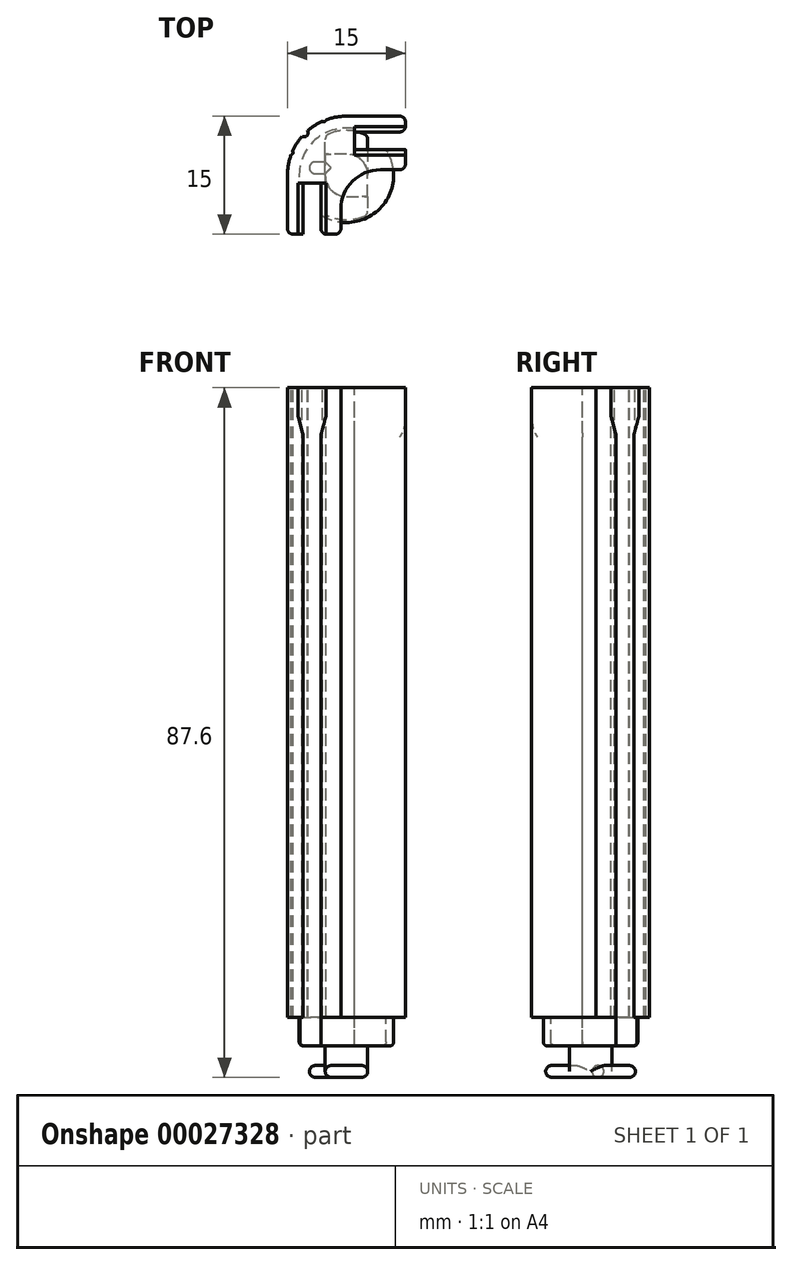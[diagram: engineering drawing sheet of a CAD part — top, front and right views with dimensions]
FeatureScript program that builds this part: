
annotation { "Feature Type Name" : "Feature", "Feature Type Description" : "" }
export const myFeature = defineFeature(function(context is Context, id is Id, definition is map)
    precondition{}
    {
        {
            var Q0;
            Q0=qCreatedBy(makeId("Top.planeOp"),FACE);
            var sketch = newSketch(context, id + "F0", { "sketchPlane" : qUnion([Q0])});
            skLineSegment(sketch, "E0", {"start": v(-7.5, -7.5) * mm, "end": v(-0.7, -7.5) * mm});
            skLineSegment(sketch, "E1", {"start": v(7.5, 0.7) * mm, "end": v(7.5, 7.5) * mm});
            skLineSegment(sketch, "E2", {"start": v(-0.7, -7.5) * mm, "end": v(-0.7, -4.3) * mm});
            skLineSegment(sketch, "E3", {"start": v(4.3, 0.7) * mm, "end": v(7.5, 0.7) * mm});
            skArc(sketch, "E4.filletArc", {"start": v(4.3, 0.7) * mm, "mid": v(0.76, -0.76) * mm, "end": v(-0.7, -4.3) * mm});
            skLineSegment(sketch, "E5", {"start": v(-7.5, -7.5) * mm, "end": v(-7.5, 0) * mm});
            skLineSegment(sketch, "E6", {"start": v(0, 7.5) * mm, "end": v(7.5, 7.5) * mm});
            skArc(sketch, "E7.filletArc", {"start": v(0, 7.5) * mm, "mid": v(-5.3, 5.3) * mm, "end": v(-7.5, 0) * mm});
            skSolve(sketch);
        }
        {
            var Q0;
            Q0 = qSketchRegion(id + "F0", true);
            extrude(context, id + "F1", {"entities" : qUnion([Q0]), "depth" : 80 * mm});
        }
        {
            var Q0;
            Q0=makeQuery(id+"F1.opExtrude","SWEPT_FACE",FACE,{"disambiguationData":[OSD([sQuery(id+"F0.wireOp",EDGE,"E0")])]});
            var sketch = newSketch(context, id + "F2", { "sketchPlane" : qUnion([Q0])});
            skLineSegment(sketch, "E8", {"start": v(-3.25, 0) * mm, "end": v(-3.25, 73.73) * mm});
            skLineSegment(sketch, "E9", {"start": v(-3.18, 74.26) * mm, "end": v(-2.64, 76.24) * mm});
            skLineSegment(sketch, "E10", {"start": v(-2.57, 76.77) * mm, "end": v(-2.57, 80) * mm});
            skPoint(sketch, "E11.visualSharp", {"position": v(-3.25, 74) * mm});
            skArc(sketch, "E11.filletArc", {"start": v(-3.18, 74.26) * mm, "mid": v(-3.23, 74) * mm, "end": v(-3.25, 73.73) * mm});
            skPoint(sketch, "E12.visualSharp", {"position": v(-2.57, 76.5) * mm});
            skArc(sketch, "E12.filletArc", {"start": v(-2.64, 76.24) * mm, "mid": v(-2.6, 76.5) * mm, "end": v(-2.57, 76.77) * mm});
            skLineSegment(sketch, "E13", {"start": v(-5.5, 0) * mm, "end": v(-3.25, 0) * mm});
            skLineSegment(sketch, "E14", {"start": v(-3.25, 0) * mm, "end": v(-5.5, 0) * mm});
            skLineSegment(sketch, "E15", {"start": v(-4.37, 0) * mm, "end": v(-4.37, 80) * mm, "construction": true});
            skLineSegment(sketch, "E16.MirrorCS", {"start": v(-5.5, 0) * mm, "end": v(-5.5, 73.73) * mm});
            skArc(sketch, "E17.MirrorCS", {"start": v(-5.57, 74.26) * mm, "mid": v(-5.52, 74) * mm, "end": v(-5.5, 73.73) * mm});
            skArc(sketch, "E18.MirrorCS", {"start": v(-6.1, 76.24) * mm, "mid": v(-6.16, 76.5) * mm, "end": v(-6.17, 76.77) * mm});
            skPoint(sketch, "E19.MirrorP", {"position": v(-5.5, 74) * mm});
            skPoint(sketch, "E20.MirrorP", {"position": v(-6.17, 76.5) * mm});
            skLineSegment(sketch, "E21.MirrorCS", {"start": v(-6.17, 76.77) * mm, "end": v(-6.17, 80) * mm});
            skLineSegment(sketch, "E22.MirrorCS", {"start": v(-5.57, 74.26) * mm, "end": v(-6.1, 76.24) * mm});
            skSolve(sketch);
        }
        {
            var Q0;
            Q0=makeQuery(id+"F2.imprint","IMPRINT",FACE,{"disambiguationData":[TD([[makeQuery(id+"F2.imprint","IMPRINT",EDGE,{"derivedFrom":sQuery(id+"F2.wireOp",EDGE,"E8")}),1.0]])]});
            extrude(context, id + "F3", {"entities" : qUnion([Q0]), "operationType" : NewBodyOperationType.REMOVE, "oppositeDirection" : true, "depth" : 6.5 * mm});
        }
        {
            var Q0;
            Q0=makeQuery(id+"F1.opExtrude","SWEPT_EDGE",EDGE,{"disambiguationData":[OSD([sQuery(id+"F0.wireOp",EDGE,"E0"),sQuery(id+"F0.wireOp",EDGE,"E2")])]});
            var Q1;
            Q1=makeQuery(id+"F3.boolean.opBoolean","COPY",EDGE,{"derivedFrom":makeQuery(id+"F3.opExtrude","CAP_EDGE",EDGE,{"disambiguationData":[OSD([sQuery(id+"F2.wireOp",EDGE,"E8")])],"isStart":true})});
            var Q2;
            Q2=makeQuery(id+"F3.boolean.opBoolean","COPY",EDGE,{"derivedFrom":makeQuery(id+"F3.opExtrude","CAP_EDGE",EDGE,{"disambiguationData":[OSD([sQuery(id+"F2.wireOp",EDGE,"60f27833-4f76-45b9-a807-f1616053afc30.MirrorCS")])],"isStart":true})});
            var Q3;
            Q3=makeQuery(id+"F1.opExtrude","SWEPT_EDGE",EDGE,{"disambiguationData":[OSD([sQuery(id+"F0.wireOp",EDGE,"E0"),sQuery(id+"F0.wireOp",EDGE,"E5")])]});
            var Q4;
            Q4=makeQuery(id+"F3.boolean.opBoolean","COPY",EDGE,{"derivedFrom":makeQuery(id+"F3.opExtrude","CAP_EDGE",EDGE,{"disambiguationData":[OSD([sQuery(id+"F2.wireOp",EDGE,"E16.MirrorCS")])],"isStart":true})});
            fillet(context, id + "F4", {"entities" : qUnion([Q0, Q1, Q2, Q3, Q4]), "radius" : 0.75 * mm, "allowEdgeOverflow" : false});
        }
        {
            var Q0;
            Q0=makeQuery(id+"F1.opExtrude","SWEPT_FACE",FACE,{"disambiguationData":[OSD([sQuery(id+"F0.wireOp",EDGE,"E1")])]});
            var sketch = newSketch(context, id + "F5", { "sketchPlane" : qUnion([Q0])});
            skLineSegment(sketch, "E23.MirrorCS", {"start": v(3.18, 74.26) * mm, "end": v(2.64, 76.24) * mm});
            skPoint(sketch, "E24.MirrorP", {"position": v(3.25, 74) * mm});
            skPoint(sketch, "E25.MirrorP", {"position": v(2.57, 76.5) * mm});
            skLineSegment(sketch, "E26.MirrorCS", {"start": v(2.57, 76.77) * mm, "end": v(2.57, 80) * mm});
            skLineSegment(sketch, "E27", {"start": v(5.57, 74.26) * mm, "end": v(6.1, 76.24) * mm});
            skLineSegment(sketch, "E28", {"start": v(6.18, 76.77) * mm, "end": v(6.18, 80) * mm});
            skPoint(sketch, "E29.visualSharp", {"position": v(5.5, 74) * mm});
            skPoint(sketch, "E30.visualSharp", {"position": v(6.18, 76.5) * mm});
            skArc(sketch, "E31.MirrorCS", {"start": v(3.18, 74.26) * mm, "mid": v(3.23, 74) * mm, "end": v(3.25, 73.73) * mm});
            skArc(sketch, "E32.MirrorCS", {"start": v(2.64, 76.24) * mm, "mid": v(2.6, 76.5) * mm, "end": v(2.57, 76.77) * mm});
            skArc(sketch, "E30.filletArc", {"start": v(6.1, 76.24) * mm, "mid": v(6.16, 76.5) * mm, "end": v(6.18, 76.77) * mm});
            skArc(sketch, "E29.filletArc", {"start": v(5.57, 74.26) * mm, "mid": v(5.52, 74) * mm, "end": v(5.5, 73.73) * mm});
            skLineSegment(sketch, "E33", {"start": v(5.5, 0) * mm, "end": v(5.5, 73.73) * mm});
            skLineSegment(sketch, "E34", {"start": v(4.38, 0) * mm, "end": v(4.38, 24.5) * mm, "construction": true});
            skLineSegment(sketch, "E35.MirrorCS", {"start": v(3.25, 0) * mm, "end": v(3.25, 73.73) * mm});
            skLineSegment(sketch, "E36", {"start": v(5.5, 0) * mm, "end": v(3.25, 0) * mm});
            skLineSegment(sketch, "E37", {"start": v(3.25, 0) * mm, "end": v(5.5, 0) * mm});
            skSolve(sketch);
        }
        {
            var Q0;
            Q0=makeQuery(id+"F5.imprint","IMPRINT",FACE,{"disambiguationData":[TD([[makeQuery(id+"F5.imprint","IMPRINT",EDGE,{"derivedFrom":sQuery(id+"F5.wireOp",EDGE,"E23.MirrorCS")}),-1.0]])]});
            extrude(context, id + "F6", {"entities" : qUnion([Q0]), "operationType" : NewBodyOperationType.REMOVE, "oppositeDirection" : true, "depth" : 6.5 * mm});
        }
        {
            var Q0;
            Q0=makeQuery(id+"F1.opExtrude","SWEPT_EDGE",EDGE,{"disambiguationData":[OSD([sQuery(id+"F0.wireOp",EDGE,"E1"),sQuery(id+"F0.wireOp",EDGE,"E3")])]});
            var Q1;
            Q1=makeQuery(id+"F6.boolean.opBoolean","COPY",EDGE,{"derivedFrom":makeQuery(id+"F6.opExtrude","CAP_EDGE",EDGE,{"disambiguationData":[OSD([sQuery(id+"F5.wireOp",EDGE,"fac70760-1ccf-4664-8ab7-3cb3c320e3f2.MirrorCS")])],"isStart":true})});
            var Q2;
            Q2=makeQuery(id+"F6.boolean.opBoolean","COPY",EDGE,{"derivedFrom":makeQuery(id+"F6.opExtrude","CAP_EDGE",EDGE,{"disambiguationData":[OSD([sQuery(id+"F5.wireOp",EDGE,"9f08e8bf-f9da-4fc2-9655-82f690379f85")])],"isStart":true})});
            var Q3;
            Q3=makeQuery(id+"F1.opExtrude","SWEPT_EDGE",EDGE,{"disambiguationData":[OSD([sQuery(id+"F0.wireOp",EDGE,"E1"),sQuery(id+"F0.wireOp",EDGE,"E6")])]});
            var Q4;
            Q4=makeQuery(id+"F6.boolean.opBoolean","COPY",EDGE,{"derivedFrom":makeQuery(id+"F6.opExtrude","CAP_EDGE",EDGE,{"disambiguationData":[OSD([sQuery(id+"F5.wireOp",EDGE,"E33")])],"isStart":true})});
            var Q5;
            Q5=makeQuery(id+"F6.boolean.opBoolean","COPY",EDGE,{"derivedFrom":makeQuery(id+"F6.opExtrude","CAP_EDGE",EDGE,{"disambiguationData":[OSD([sQuery(id+"F5.wireOp",EDGE,"E35.MirrorCS")])],"isStart":true})});
            fillet(context, id + "F7", {"entities" : qUnion([Q0, Q1, Q2, Q3, Q4, Q5]), "radius" : 0.75 * mm, "allowEdgeOverflow" : false});
        }
        {
            var Q0;
            Q0=makeQuery(id+"F1.opExtrude","CAP_FACE",FACE,{"disambiguationData":[OSD([sQuery(id+"F0.wireOp",EDGE,"E0"),sQuery(id+"F0.wireOp",EDGE,"E1"),sQuery(id+"F0.wireOp",EDGE,"E2"),sQuery(id+"F0.wireOp",EDGE,"E3"),sQuery(id+"F0.wireOp",EDGE,"E4.filletArc"),sQuery(id+"F0.wireOp",EDGE,"E5"),sQuery(id+"F0.wireOp",EDGE,"E6"),sQuery(id+"F0.wireOp",EDGE,"E7.filletArc")])],"isStart":true});
            var sketch = newSketch(context, id + "F8", { "sketchPlane" : qUnion([Q0])});
            skCircle(sketch, "E38", {"center": v(0, 0) * mm, "radius": 6 * mm, "construction": true});
            skLineSegment(sketch, "E39", {"start": v(-3.25, 5.04) * mm, "end": v(-3.25, 1) * mm});
            skLineSegment(sketch, "E40", {"start": v(-3.25, 1) * mm, "end": v(-5.92, 1) * mm});
            skLineSegment(sketch, "E41", {"start": v(5.04, -3.25) * mm, "end": v(1, -3.25) * mm});
            skLineSegment(sketch, "E42", {"start": v(1, -3.25) * mm, "end": v(1, -5.92) * mm});
            skArc(sketch, "E43", {"start": v(-5.92, 1) * mm, "mid": v(-4.24, -4.24) * mm, "end": v(1, -5.92) * mm});
            skArc(sketch, "E44", {"start": v(5.04, -3.25) * mm, "mid": v(4.24, 4.24) * mm, "end": v(-3.25, 5.04) * mm});
            skSolve(sketch);
        }
        {
            var Q0;
            {var subQ8=sQuery(id+"F8.wireOp",EDGE,"E39");Q0=makeQuery(id+"F8.imprint","IMPRINT",FACE,{"disambiguationData":[TD([[makeQuery(id+"F8.imprint","IMPRINT",EDGE,{"derivedFrom":subQ8}),-1.0]])]});}
            var Q1;
            {var subQ3=makeQuery(id+"F1.opExtrude","CAP_EDGE",EDGE,{"disambiguationData":[OSD([sQuery(id+"F0.wireOp",EDGE,"E4.filletArc")])],"isStart":true});Q1=makeQuery(id+"F8.imprint","IMPRINT",FACE,{"disambiguationData":[TD([[makeQuery(id+"F8.imprint","IMPRINT",EDGE,{"derivedFrom":subQ3}),-1.0]])]});}
            extrude(context, id + "F9", {"entities" : qUnion([Q0, Q1]), "operationType" : NewBodyOperationType.ADD, "depth" : 3.6 * mm});
        }
        {
            var Q0;
            Q0=makeQuery(id+"F9.opExtrude","CAP_FACE",FACE,{"disambiguationData":[OSD([sQuery(id+"F8.wireOp",EDGE,"E38"),sQuery(id+"F8.wireOp",EDGE,"a5d605d6-822f-4dd6-a2a0-b089b62b14bf"),sQuery(id+"F8.wireOp",EDGE,"013d6ad0-5a63-439a-87f6-5f468e9a351e"),sQuery(id+"F8.wireOp",EDGE,"E39"),sQuery(id+"F8.wireOp",EDGE,"E40")])],"isStart":false});
            var sketch = newSketch(context, id + "F10", { "sketchPlane" : qUnion([Q0])});
            skCircle(sketch, "E45", {"center": v(0, 0) * mm, "radius": 2.7 * mm});
            skPoint(sketch, "E46", {"position": v(0, -2.7) * mm});
            skPoint(sketch, "E47", {"position": v(0, 2.7) * mm});
            skLineSegment(sketch, "E48", {"start": v(0, -2.7) * mm, "end": v(0, 2.7) * mm});
            skLineSegment(sketch, "E49", {"start": v(0, -2.7) * mm, "end": v(-2.7, -2.7) * mm});
            skLineSegment(sketch, "E50", {"start": v(-2.7, -2.7) * mm, "end": v(-2.7, 0) * mm});
            skLineSegment(sketch, "E51", {"start": v(0, 2.7) * mm, "end": v(2.7, 2.7) * mm});
            skLineSegment(sketch, "E52", {"start": v(2.7, 2.7) * mm, "end": v(2.7, 0) * mm});
            skSolve(sketch);
        }
        {
            var Q0;
            Q0 = qSketchRegion(id + "F10", true);
            extrude(context, id + "F11", {"entities" : qUnion([Q0]), "operationType" : NewBodyOperationType.ADD, "depth" : 2.5 * mm});
        }
        {
            var Q0;
            Q0=makeQuery(id+"F11.opExtrude","CAP_FACE",FACE,{"disambiguationData":[OSD([sQuery(id+"F10.wireOp",EDGE,"E45"),sQuery(id+"F10.wireOp",EDGE,"E49"),sQuery(id+"F10.wireOp",EDGE,"E50"),sQuery(id+"F10.wireOp",EDGE,"E51"),sQuery(id+"F10.wireOp",EDGE,"E52")])],"isStart":false});
            var sketch = newSketch(context, id + "F12", { "sketchPlane" : qUnion([Q0])});
            skLineSegment(sketch, "E53", {"start": v(0, 0) * mm, "end": v(-2.7, 0) * mm, "construction": true});
            skLineSegment(sketch, "E54", {"start": v(-2.7, 5.02) * mm, "end": v(-2.7, -5.02) * mm});
            skLineSegment(sketch, "E55", {"start": v(0, 0.95) * mm, "end": v(0, 0) * mm, "construction": true});
            skLineSegment(sketch, "E56.MirrorCS", {"start": v(2.7, 5.02) * mm, "end": v(2.7, -5.02) * mm});
            skArc(sketch, "E57", {"start": v(-2.7, -5.02) * mm, "mid": v(0, -5.7) * mm, "end": v(2.7, -5.02) * mm});
            skArc(sketch, "E58.MirrorCS", {"start": v(-2.7, 5.02) * mm, "mid": v(0, 5.7) * mm, "end": v(2.7, 5.02) * mm});
            skSolve(sketch);
        }
        {
            var Q0;
            Q0 = qSketchRegion(id + "F12", true);
            extrude(context, id + "F13", {"entities" : qUnion([Q0]), "operationType" : NewBodyOperationType.ADD, "depth" : 1.5 * mm});
        }
        {
            var Q0;
            Q0=makeQuery(id+"F13.opExtrude","SWEPT_FACE",FACE,{"disambiguationData":[OSD([sQuery(id+"F12.wireOp",EDGE,"E54")])]});
            var sketch = newSketch(context, id + "F14", { "sketchPlane" : qUnion([Q0])});
            skLineSegment(sketch, "E59", {"start": v(-0.95, -6.1) * mm, "end": v(-0.95, -7.6) * mm});
            skLineSegment(sketch, "E60", {"start": v(-0.95, -6.1) * mm, "end": v(0, -6.1) * mm});
            skPoint(sketch, "E61", {"position": v(-0.95, -6.85) * mm});
            skCircle(sketch, "E62", {"center": v(-0.95, -6.85) * mm, "radius": 0.75 * mm});
            skSolve(sketch);
        }
        {
            var Q0;
            Q0 = qSketchRegion(id + "F14", true);
            extrude(context, id + "F15", {"entities" : qUnion([Q0]), "operationType" : NewBodyOperationType.ADD, "depth" : 2 * mm, "hasSecondDirection" : true, "secondDirectionOppositeDirection" : true, "secondDirectionDepth" : 2 * mm});
        }
        {
            var Q0;
            Q0=makeQuery(id+"F13.opExtrude","CAP_EDGE",EDGE,{"disambiguationData":[OSD([sQuery(id+"F12.wireOp",EDGE,"E56.MirrorCS")])],"isStart":false});
            var Q1;
            Q1=makeQuery(id+"F13.opExtrude","SWEPT_EDGE",EDGE,{"disambiguationData":[OSD([sQuery(id+"F12.wireOp",EDGE,"E56.MirrorCS"),sQuery(id+"F12.wireOp",EDGE,"E58.MirrorCS")])]});
            var Q2;
            Q2=makeQuery(id+"F13.opExtrude","CAP_EDGE",EDGE,{"disambiguationData":[OSD([sQuery(id+"F12.wireOp",EDGE,"E58.MirrorCS")])],"isStart":false});
            var Q3;
            Q3=makeQuery(id+"F13.opExtrude","SWEPT_EDGE",EDGE,{"disambiguationData":[OSD([sQuery(id+"F12.wireOp",EDGE,"E56.MirrorCS"),sQuery(id+"F12.wireOp",EDGE,"E57")])]});
            var Q4;
            Q4=makeQuery(id+"F13.opExtrude","CAP_EDGE",EDGE,{"disambiguationData":[OSD([sQuery(id+"F12.wireOp",EDGE,"E57")])],"isStart":false});
            var Q5;
            Q5=makeQuery(id+"F13.opExtrude","CAP_EDGE",EDGE,{"disambiguationData":[OSD([sQuery(id+"F12.wireOp",EDGE,"E54")])],"isStart":false});
            var Q6;
            Q6=makeQuery(id+"F13.opExtrude","SWEPT_EDGE",EDGE,{"disambiguationData":[OSD([sQuery(id+"F12.wireOp",EDGE,"E54"),sQuery(id+"F12.wireOp",EDGE,"E58.MirrorCS")])]});
            var Q7;
            Q7=makeQuery(id+"F13.opExtrude","SWEPT_EDGE",EDGE,{"disambiguationData":[OSD([sQuery(id+"F12.wireOp",EDGE,"E54"),sQuery(id+"F12.wireOp",EDGE,"E57")])]});
            var Q8;
            {var subQ0=sQuery(id+"F12.wireOp",EDGE,"E56.MirrorCS");var subQ1=sQuery(id+"F12.wireOp",EDGE,"E57");var subQ2=sQuery(id+"F10.wireOp",EDGE,"E52");Q8=makeQuery(id+"F13.boolean.opBoolean","SPLIT",EDGE,{"disambiguationData":[TD([makeQuery(id+"F11.opExtrude","CAP_FACE",FACE,{"disambiguationData":[OSD([sQuery(id+"F10.wireOp",EDGE,"E45"),sQuery(id+"F10.wireOp",EDGE,"E49"),sQuery(id+"F10.wireOp",EDGE,"E50"),sQuery(id+"F10.wireOp",EDGE,"E51"),subQ2])],"isStart":false}),makeQuery(id+"F11.opExtrude","SWEPT_FACE",FACE,{"disambiguationData":[OSD([subQ2])]}),makeQuery(id+"F13.opExtrude","CAP_FACE",FACE,{"disambiguationData":[OSD([sQuery(id+"F12.wireOp",EDGE,"E54"),subQ0,subQ1,sQuery(id+"F12.wireOp",EDGE,"E58.MirrorCS")])],"isStart":true}),makeQuery(id+"F13.opExtrude","SWEPT_FACE",FACE,{"disambiguationData":[OSD([subQ0])]}),makeQuery(id+"F13.opExtrude","SWEPT_FACE",FACE,{"disambiguationData":[OSD([subQ1])]})])],"derivedFrom":makeQuery(id+"F13.opExtrude","CAP_EDGE",EDGE,{"disambiguationData":[OSD([subQ0])],"isStart":true})});}
            var Q9;
            {var subQ0=sQuery(id+"F12.wireOp",EDGE,"E56.MirrorCS");var subQ1=sQuery(id+"F12.wireOp",EDGE,"E58.MirrorCS");var subQ2=sQuery(id+"F10.wireOp",EDGE,"E51");Q9=makeQuery(id+"F13.boolean.opBoolean","SPLIT",EDGE,{"disambiguationData":[TD([makeQuery(id+"F11.opExtrude","CAP_FACE",FACE,{"disambiguationData":[OSD([sQuery(id+"F10.wireOp",EDGE,"E45"),sQuery(id+"F10.wireOp",EDGE,"E49"),sQuery(id+"F10.wireOp",EDGE,"E50"),subQ2,sQuery(id+"F10.wireOp",EDGE,"E52")])],"isStart":false}),makeQuery(id+"F11.opExtrude","SWEPT_FACE",FACE,{"disambiguationData":[OSD([subQ2])]}),makeQuery(id+"F13.opExtrude","CAP_FACE",FACE,{"disambiguationData":[OSD([sQuery(id+"F12.wireOp",EDGE,"E54"),subQ0,sQuery(id+"F12.wireOp",EDGE,"E57"),subQ1])],"isStart":true}),makeQuery(id+"F13.opExtrude","SWEPT_FACE",FACE,{"disambiguationData":[OSD([subQ0])]}),makeQuery(id+"F13.opExtrude","SWEPT_FACE",FACE,{"disambiguationData":[OSD([subQ1])]})])],"derivedFrom":makeQuery(id+"F13.opExtrude","CAP_EDGE",EDGE,{"disambiguationData":[OSD([subQ0])],"isStart":true})});}
            var Q10;
            Q10=makeQuery(id+"F13.opExtrude","CAP_EDGE",EDGE,{"disambiguationData":[OSD([sQuery(id+"F12.wireOp",EDGE,"E58.MirrorCS")])],"isStart":true});
            var Q11;
            {var subQ0=sQuery(id+"F12.wireOp",EDGE,"E54");var subQ1=sQuery(id+"F12.wireOp",EDGE,"E58.MirrorCS");var subQ2=sQuery(id+"F10.wireOp",EDGE,"E50");Q11=makeQuery(id+"F13.boolean.opBoolean","SPLIT",EDGE,{"disambiguationData":[TD([makeQuery(id+"F11.opExtrude","CAP_FACE",FACE,{"disambiguationData":[OSD([sQuery(id+"F10.wireOp",EDGE,"E45"),sQuery(id+"F10.wireOp",EDGE,"E49"),subQ2,sQuery(id+"F10.wireOp",EDGE,"E51"),sQuery(id+"F10.wireOp",EDGE,"E52")])],"isStart":false}),makeQuery(id+"F11.opExtrude","SWEPT_FACE",FACE,{"disambiguationData":[OSD([subQ2])]}),makeQuery(id+"F13.opExtrude","SWEPT_FACE",FACE,{"disambiguationData":[OSD([subQ0])]}),makeQuery(id+"F13.opExtrude","CAP_FACE",FACE,{"disambiguationData":[OSD([subQ0,sQuery(id+"F12.wireOp",EDGE,"E56.MirrorCS"),sQuery(id+"F12.wireOp",EDGE,"E57"),subQ1])],"isStart":true}),makeQuery(id+"F13.opExtrude","SWEPT_FACE",FACE,{"disambiguationData":[OSD([subQ1])]})])],"derivedFrom":makeQuery(id+"F13.opExtrude","CAP_EDGE",EDGE,{"disambiguationData":[OSD([subQ0])],"isStart":true})});}
            var Q12;
            Q12=makeQuery(id+"F13.opExtrude","CAP_EDGE",EDGE,{"disambiguationData":[OSD([sQuery(id+"F12.wireOp",EDGE,"E57")])],"isStart":true});
            var Q13;
            {var subQ0=sQuery(id+"F12.wireOp",EDGE,"E54");var subQ1=sQuery(id+"F12.wireOp",EDGE,"E57");var subQ2=sQuery(id+"F10.wireOp",EDGE,"E49");Q13=makeQuery(id+"F13.boolean.opBoolean","SPLIT",EDGE,{"disambiguationData":[TD([makeQuery(id+"F11.opExtrude","CAP_FACE",FACE,{"disambiguationData":[OSD([sQuery(id+"F10.wireOp",EDGE,"E45"),subQ2,sQuery(id+"F10.wireOp",EDGE,"E50"),sQuery(id+"F10.wireOp",EDGE,"E51"),sQuery(id+"F10.wireOp",EDGE,"E52")])],"isStart":false}),makeQuery(id+"F11.opExtrude","SWEPT_FACE",FACE,{"disambiguationData":[OSD([subQ2])]}),makeQuery(id+"F13.opExtrude","SWEPT_FACE",FACE,{"disambiguationData":[OSD([subQ0])]}),makeQuery(id+"F13.opExtrude","CAP_FACE",FACE,{"disambiguationData":[OSD([subQ0,sQuery(id+"F12.wireOp",EDGE,"E56.MirrorCS"),subQ1,sQuery(id+"F12.wireOp",EDGE,"E58.MirrorCS")])],"isStart":true}),makeQuery(id+"F13.opExtrude","SWEPT_FACE",FACE,{"disambiguationData":[OSD([subQ1])]})])],"derivedFrom":makeQuery(id+"F13.opExtrude","CAP_EDGE",EDGE,{"disambiguationData":[OSD([subQ0])],"isStart":true})});}
            var Q14;
            Q14=makeQuery(id+"F15.opExtrude","CAP_EDGE",EDGE,{"disambiguationData":[OSD([sQuery(id+"F14.wireOp",EDGE,"E62")])],"isStart":false});
            fillet(context, id + "F16", {"entities" : qUnion([Q0, Q1, Q2, Q3, Q4, Q5, Q6, Q7, Q8, Q9, Q10, Q11, Q12, Q13, Q14]), "radius" : 0.75 * mm, "tangentPropagation" : true, "allowEdgeOverflow" : false});
        }
        {
            var Q0;
            Q0=makeQuery(id+"F9.opExtrude","CAP_EDGE",EDGE,{"disambiguationData":[OSD([sQuery(id+"F8.wireOp",EDGE,"E44")])],"isStart":false});
            var Q1;
            Q1=makeQuery(id+"F9.opExtrude","CAP_EDGE",EDGE,{"disambiguationData":[OSD([sQuery(id+"F8.wireOp",EDGE,"E43")])],"isStart":false});
            fillet(context, id + "F17", {"entities" : qUnion([Q0, Q1]), "radius" : 0.5 * mm, "tangentPropagation" : true, "allowEdgeOverflow" : false});
        }
        {
            var Q0;
            Q0=makeQuery(id+"F1.opExtrude","CAP_FACE",FACE,{"disambiguationData":[OSD([sQuery(id+"F0.wireOp",EDGE,"E0"),sQuery(id+"F0.wireOp",EDGE,"E1"),sQuery(id+"F0.wireOp",EDGE,"E2"),sQuery(id+"F0.wireOp",EDGE,"E3"),sQuery(id+"F0.wireOp",EDGE,"E4.filletArc"),sQuery(id+"F0.wireOp",EDGE,"E5"),sQuery(id+"F0.wireOp",EDGE,"E6"),sQuery(id+"F0.wireOp",EDGE,"E7.filletArc")])],"isStart":false});
            var sketch = newSketch(context, id + "F18", { "sketchPlane" : qUnion([Q0])});
            skArc(sketch, "E63", {"start": v(0, 7.6) * mm, "mid": v(-5.37, 5.37) * mm, "end": v(-7.6, 0) * mm});
            skPoint(sketch, "E64", {"position": v(-5.37, 5.37) * mm});
            skCircle(sketch, "E65", {"center": v(-5.37, 5.37) * mm, "radius": 0.5 * mm});
            skCircle(sketch, "E66", {"center": v(-7.03, 2.88) * mm, "radius": 0.25 * mm});
            skLineSegment(sketch, "E67", {"start": v(-5.37, 5.37) * mm, "end": v(0, 0) * mm, "construction": true});
            skCircle(sketch, "E68.MirrorC", {"center": v(-2.88, 7.03) * mm, "radius": 0.25 * mm});
            skSolve(sketch);
        }
        {
            var Q0;
            Q0 = qSketchRegion(id + "F18", true);
            extrude(context, id + "F19", {"entities" : qUnion([Q0]), "operationType" : NewBodyOperationType.REMOVE, "oppositeDirection" : true, "depth" : 80 * mm});
        }
    });
